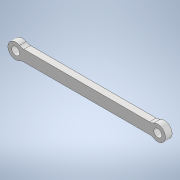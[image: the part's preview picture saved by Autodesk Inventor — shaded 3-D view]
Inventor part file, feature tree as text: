
AUTODESK INVENTOR PART (.ipt)
format: ipt  version: 2020 (Build 240168000, 168)  size: 126,464 bytes
history: native  units: mm
features: extrude x1, fillet x1, sketch x1
ambient origin geometry x8: Origin, YZ Plane, XZ Plane, XY Plane, X Axis, Y Axis, Z Axis, Center Point
bodies: Solid1 (feature_tree)
feature tree (3):
  extrude  "Extrusion1"  Depth=4.0mm
  fillet  "Fillet2"  Radius=1.5mm
  sketch  "Sketch1"  dims[d0=2.0mm d1=4.0mm d4=1.5mm d5=0.0mm d8=3.0mm d9=32.3mm d10=2.0mm]
